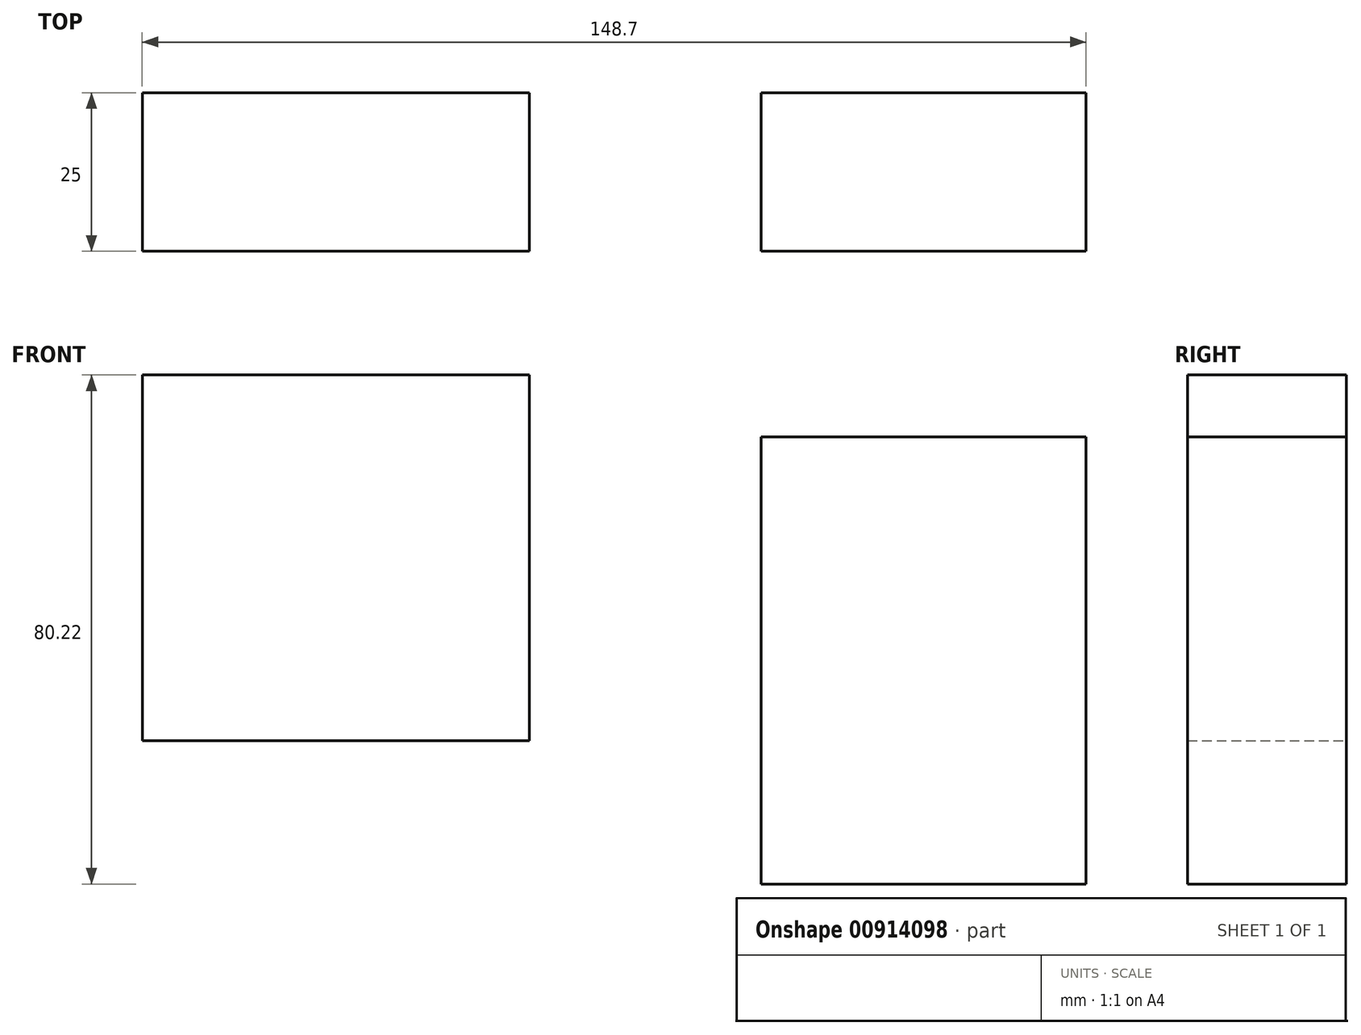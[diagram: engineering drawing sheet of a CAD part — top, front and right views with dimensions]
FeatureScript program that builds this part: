
annotation { "Feature Type Name" : "Feature", "Feature Type Description" : "" }
export const myFeature = defineFeature(function(context is Context, id is Id, definition is map)
    precondition{}
    {
        {
            var Q0;
            Q0=qCreatedBy(makeId("Front.planeOp"),FACE);
            var sketch = newSketch(context, id + "F0", { "sketchPlane" : qUnion([Q0])});
            skLineSegment(sketch, "E0.bottom", {"start": v(-148.7, 39.9) * mm, "end": v(-87.68, 39.9) * mm});
            skLineSegment(sketch, "E0.top", {"start": v(-148.7, -17.75) * mm, "end": v(-87.68, -17.75) * mm});
            skLineSegment(sketch, "E0.left", {"start": v(-148.7, 39.9) * mm, "end": v(-148.7, -17.75) * mm});
            skLineSegment(sketch, "E0.right", {"start": v(-87.68, 39.9) * mm, "end": v(-87.68, -17.75) * mm});
            skLineSegment(sketch, "E1.bottom", {"start": v(-51.18, 30.13) * mm, "end": v(0, 30.13) * mm});
            skLineSegment(sketch, "E1.top", {"start": v(-51.18, -40.3) * mm, "end": v(0, -40.3) * mm});
            skLineSegment(sketch, "E1.left", {"start": v(-51.18, 30.13) * mm, "end": v(-51.18, -40.3) * mm});
            skLineSegment(sketch, "E1.right", {"start": v(0, 30.13) * mm, "end": v(0, -40.3) * mm});
            skSolve(sketch);
        }
        {
            var Q0;
            Q0 = qSketchRegion(id + "F0", true);
            extrude(context, id + "F1", {"entities" : qUnion([Q0]), "depth" : 25 * mm, "offsetDistance" : 25 * mm});
        }
    });
